# Revit family: 511_AWN-AU_stucco key
name_source: partatom
category: Windows
revit_build: Autodesk Revit 2016 (Build: 20150220_1215(x64)
units: mm (PartAtom-declared; Revit-internal decimal feet)

## family parameters
Always vertical = Yes
Cut with Voids When Loaded = No
Host = Wall
OmniClass Number = 23.30.20.00
OmniClass Title = Windows
Room Calculation Point = No
Shared = No

## types (54) — shared parameters
Default Sill Height = 31 1/2"
MLW = 3 3/16"
Wall Closure = By host

## per-type parameters (varying)
| type | BSA | BSU | Height | MLH | MLW2 | MLW3 | Width |
| 15x36Min | 12" | 12" | 36" | 7 1/2" | 1 1/2" | 1 1/2" | 15" |
| 36x72 | 24" | 24" | 72" | 18" | 3" | 3" | 36" |
| 48x120Max | 44" | 44" | 120" | 24" | 5 1/2" | 5 1/2" | 48" |
| 24x48 | 16" | 16" | 48" | 12" | 2" | 2" | 24" |
| 24x36 | 12" | 12" | 36" | 12" | 1 1/2" | 1 1/2" | 24" |
| 24x42 | 12" | 12" | 42" | 12" | 1 1/2" | 1 1/2" | 24" |
| 24x54 | 18" | 18" | 54" | 12" | 2 1/4" | 2 1/4" | 24" |
| 24x60 | 20" | 20" | 60" | 12" | 2 1/2" | 2 1/2" | 24" |
| 24x66 | 22" | 22" | 66" | 12" | 2 3/4" | 2 3/4" | 24" |
| 24x72 | 24" | 24" | 72" | 12" | 3" | 3" | 24" |
| 24x78 | 24" | 24" | 78" | 12" | 3" | 3" | 24" |
| 24x84 | 30" | 30" | 84" | 12" | 3 3/4" | 3 3/4" | 24" |
| 30x36 | 12" | 12" | 36" | 15" | 1 1/2" | 1 1/2" | 30" |
| 30x42 | 12" | 12" | 42" | 15" | 1 1/2" | 1 1/2" | 30" |
| 30x48 | 12" | 12" | 42" | 15" | 1 1/2" | 1 1/2" | 30" |
| 30x54 | 18" | 18" | 54" | 15" | 2 1/4" | 2 1/4" | 30" |
| 30x60 | 20" | 20" | 60" | 15" | 2 1/2" | 2 1/2" | 30" |
| 30x66 | 22" | 22" | 66" | 15" | 2 3/4" | 2 3/4" | 30" |
| 30x72 | 24" | 24" | 72" | 15" | 3" | 3" | 30" |
| 30x78 | 24" | 24" | 78" | 15" | 3" | 3" | 30" |
| 30x84 | 30" | 30" | 84" | 15" | 3 3/4" | 3 3/4" | 30" |
| 36x42 | 12" | 12" | 42" | 18" | 1 1/2" | 1 1/2" | 36" |
| 36x48 | 16" | 16" | 48" | 18" | 2" | 2" | 36" |
| 36x54 | 18" | 18" | 54" | 18" | 2 1/4" | 2 1/4" | 36" |
| 36x60 | 20" | 20" | 60" | 18" | 2 1/2" | 2 1/2" | 36" |
| 36x66 | 22" | 22" | 66" | 18" | 2 3/4" | 2 3/4" | 36" |
| 36x78 | 26" | 26" | 78" | 18" | 3 1/4" | 3 1/4" | 36" |
| 36x84 | 30" | 30" | 84" | 18" | 3 3/4" | 3 3/4" | 36" |
| 36x90 | 30" | 30" | 90" | 18" | 3 3/4" | 3 3/4" | 36" |
| 42x48 | 16" | 16" | 48" | 21" | 2" | 2" | 42" |
| 42x54 | 18" | 18" | 54" | 21" | 2 1/4" | 2 1/4" | 42" |
| 42x60 | 20" | 20" | 60" | 21" | 2 1/2" | 2 1/2" | 42" |
| 42x66 | 22" | 22" | 66" | 21" | 2 3/4" | 2 3/4" | 42" |
| 42x72 | 24" | 24" | 72" | 21" | 3" | 3" | 42" |
| 42x78 | 26" | 26" | 78" | 21" | 3 1/4" | 3 1/4" | 42" |
| 42x84 | 28" | 28" | 84" | 21" | 3 1/2" | 3 1/2" | 42" |
| 42x90 | 30" | 30" | 90" | 21" | 3 3/4" | 3 3/4" | 42" |
| 42x96 | 32" | 32" | 96" | 21" | 4" | 4" | 42" |
| 42x102 | 36" | 36" | 102" | 21" | 4 1/2" | 4 1/2" | 42" |
| 42x108 | 38" | 38" | 108" | 21" | 4 3/4" | 4 3/4" | 42" |
| 42x114 | 42" | 42" | 114" | 21" | 5 1/4" | 5 1/4" | 42" |
| 42x120 | 44" | 44" | 120" | 21" | 5 1/2" | 5 1/2" | 42" |
| 48x48 | 12" | 12" | 48" | 24" | 1 1/2" | 1 1/2" | 48" |
| 48x54 | 18" | 18" | 54" | 24" | 2 1/4" | 2 1/4" | 48" |
| 48x60 | 20" | 20" | 60" | 24" | 2 1/2" | 2 1/2" | 48" |
| 48x66 | 22" | 22" | 66" | 24" | 2 3/4" | 2 3/4" | 48" |
| 48x72 | 24" | 24" | 72" | 24" | 3" | 3" | 48" |
| 48x78 | 26" | 26" | 78" | 24" | 3 1/4" | 3 1/4" | 48" |
| 48x84 | 28" | 28" | 84" | 24" | 3 1/2" | 3 1/2" | 48" |
| 48x90 | 30" | 30" | 90" | 24" | 3 3/4" | 3 3/4" | 48" |
| 48x96 | 32" | 32" | 96" | 24" | 4" | 4" | 48" |
| 48x102 | 36" | 36" | 102" | 24" | 4 1/2" | 4 1/2" | 48" |
| 48x108 | 38" | 38" | 108" | 24" | 4 3/4" | 4 3/4" | 48" |
| 48x114 | 42" | 42" | 114" | 24" | 5 1/4" | 5 1/4" | 48" |

## geometry (parser evidence)
native form markers: Sweep x2
no freeform markers — native parametric forms only
